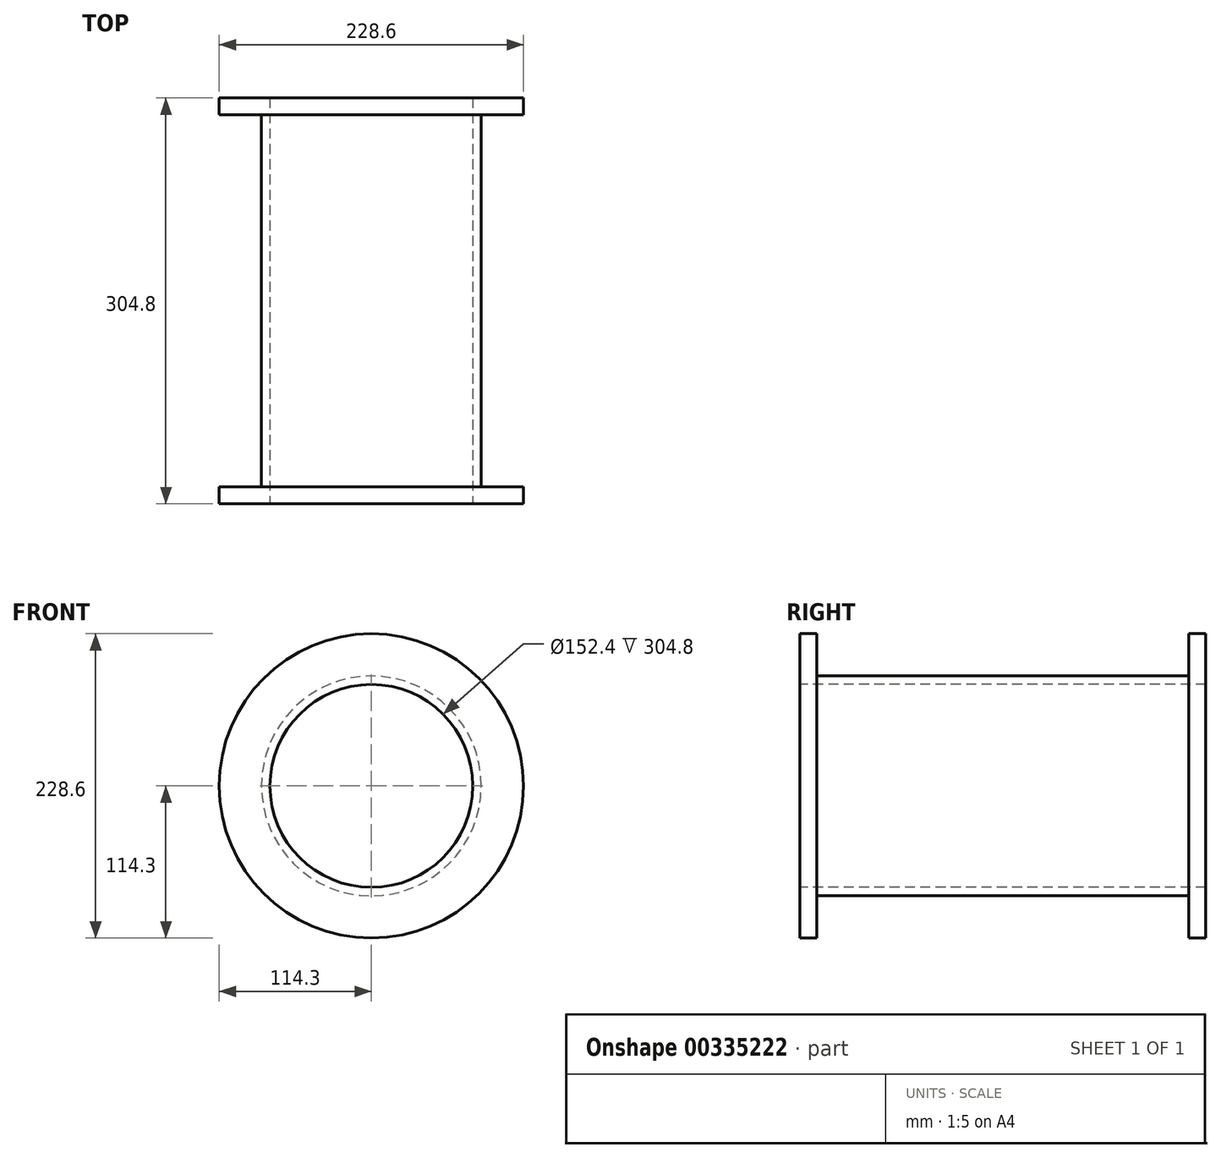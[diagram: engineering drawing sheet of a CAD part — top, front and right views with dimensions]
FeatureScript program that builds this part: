
annotation { "Feature Type Name" : "Feature", "Feature Type Description" : "" }
export const myFeature = defineFeature(function(context is Context, id is Id, definition is map)
    precondition{}
    {
        {
            var Q0;
            Q0=qCreatedBy(makeId("Right.planeOp"),FACE);
            var sketch = newSketch(context, id + "F0", { "sketchPlane" : qUnion([Q0])});
            skLineSegment(sketch, "E0", {"start": v(-372.41, 0) * mm, "end": v(512.39, 0) * mm, "construction": true});
            skLineSegment(sketch, "E1", {"start": v(0, 114.3) * mm, "end": v(-12.7, 114.3) * mm});
            skLineSegment(sketch, "E2", {"start": v(-12.7, 114.3) * mm, "end": v(-12.7, 82.55) * mm});
            skLineSegment(sketch, "E3", {"start": v(-12.7, 82.55) * mm, "end": v(-292.1, 82.55) * mm});
            skLineSegment(sketch, "E4", {"start": v(-292.1, 82.55) * mm, "end": v(-292.1, 114.3) * mm});
            skLineSegment(sketch, "E5", {"start": v(-292.1, 114.3) * mm, "end": v(-304.8, 114.3) * mm});
            skLineSegment(sketch, "E6", {"start": v(-304.8, 76.2) * mm, "end": v(304.8, 76.2) * mm});
            skLineSegment(sketch, "E7", {"start": v(-304.8, 114.3) * mm, "end": v(-304.8, 76.2) * mm});
            skLineSegment(sketch, "E8", {"start": v(0, 114.3) * mm, "end": v(0, 76.2) * mm});
            skSolve(sketch);
        }
        {
            var Q0;
            Q0=makeQuery(id+"F0.imprint","IMPRINT",FACE,{"disambiguationData":[TD([[makeQuery(id+"F0.imprint","IMPRINT",EDGE,{"derivedFrom":sQuery(id+"F0.wireOp",EDGE,"E1")}),1.0]])]});
            var Q1;
            Q1=sQuery(id+"F0.wireOp",EDGE,"E0");
            revolve(context, id + "F1", {"entities" : qUnion([Q0]), "axis" : qUnion([Q1]), "revolveType" : RevolveType.FULL});
        }
    });
